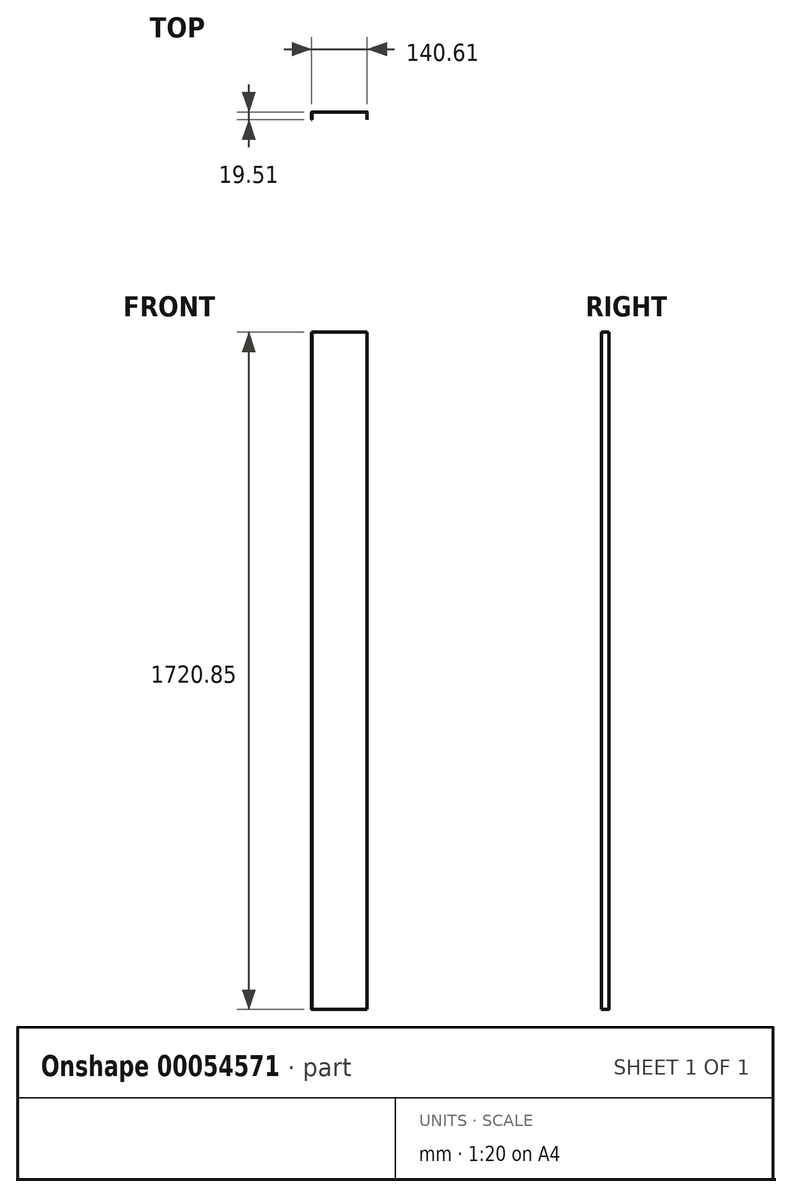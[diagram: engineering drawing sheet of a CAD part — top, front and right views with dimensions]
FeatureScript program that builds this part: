
annotation { "Feature Type Name" : "Feature", "Feature Type Description" : "" }
export const myFeature = defineFeature(function(context is Context, id is Id, definition is map)
    precondition{}
    {
        {
            var Q0;
            Q0=qCreatedBy(makeId("Top.planeOp"),FACE);
            var sketch = newSketch(context, id + "F0", { "sketchPlane" : qUnion([Q0])});
            skLineSegment(sketch, "E0", {"start": v(0.25, 0) * mm, "end": v(140.36, 0) * mm});
            skLineSegment(sketch, "E1", {"start": v(140.61, -0.25) * mm, "end": v(140.61, -19.5) * mm});
            skLineSegment(sketch, "E2", {"start": v(0, -0.25) * mm, "end": v(0, -19.5) * mm});
            skLineSegment(sketch, "E3", {"start": v(0.46, -19.5) * mm, "end": v(0.46, -0.71) * mm});
            skLineSegment(sketch, "E4", {"start": v(0.71, -0.46) * mm, "end": v(139.9, -0.46) * mm});
            skLineSegment(sketch, "E5", {"start": v(140.16, -0.71) * mm, "end": v(140.16, -19.5) * mm});
            skLineSegment(sketch, "E6", {"start": v(0, -19.5) * mm, "end": v(0.46, -19.5) * mm});
            skLineSegment(sketch, "E7", {"start": v(140.16, -19.5) * mm, "end": v(140.61, -19.5) * mm});
            skPoint(sketch, "E8.visualSharp", {"position": v(0.46, -0.46) * mm});
            skArc(sketch, "E8.filletArc", {"start": v(0.71, -0.46) * mm, "mid": v(0.53, -0.53) * mm, "end": v(0.46, -0.71) * mm});
            skPoint(sketch, "E9.visualSharp", {"position": v(0, 0) * mm});
            skArc(sketch, "E9.filletArc", {"start": v(0.25, 0) * mm, "mid": v(0.07, -0.07) * mm, "end": v(0, -0.25) * mm});
            skPoint(sketch, "E10.visualSharp", {"position": v(140.16, -0.46) * mm});
            skArc(sketch, "E10.filletArc", {"start": v(140.16, -0.71) * mm, "mid": v(140.08, -0.53) * mm, "end": v(139.9, -0.46) * mm});
            skPoint(sketch, "E11.visualSharp", {"position": v(140.61, 0) * mm});
            skArc(sketch, "E11.filletArc", {"start": v(140.61, -0.25) * mm, "mid": v(140.54, -0.07) * mm, "end": v(140.36, 0) * mm});
            skSolve(sketch);
        }
        {
            var Q0;
            Q0=makeQuery(id+"F0.imprint","IMPRINT",FACE,{"disambiguationData":[TD([[makeQuery(id+"F0.imprint","IMPRINT",EDGE,{"derivedFrom":sQuery(id+"F0.wireOp",EDGE,"E0")}),-1.0]])]});
            extrude(context, id + "F1", {"entities" : qUnion([Q0]), "depth" : 1720.85 * mm});
        }
    });
